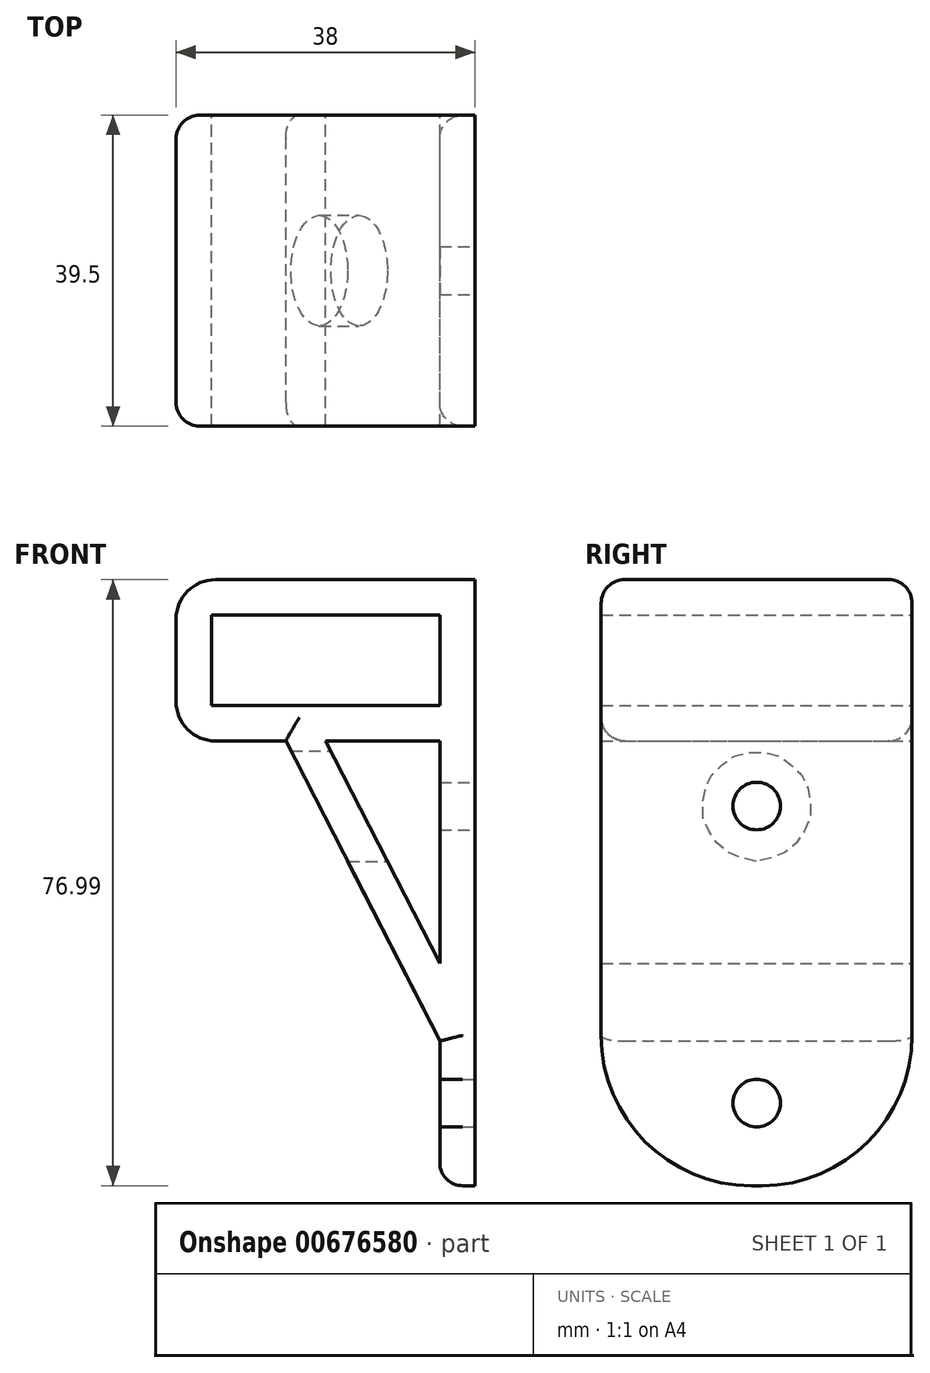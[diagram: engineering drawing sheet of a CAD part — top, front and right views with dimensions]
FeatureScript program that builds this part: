
annotation { "Feature Type Name" : "Feature", "Feature Type Description" : "" }
export const myFeature = defineFeature(function(context is Context, id is Id, definition is map)
    precondition{}
    {
        {
            var Q0;
            Q0=qCreatedBy(makeId("Front.planeOp"),FACE);
            var sketch = newSketch(context, id + "F0", { "sketchPlane" : qUnion([Q0])});
            skLineSegment(sketch, "E0.bottom", {"start": v(14.5, -5.75) * mm, "end": v(-14.5, -5.75) * mm});
            skLineSegment(sketch, "E0.top", {"start": v(14.5, 5.75) * mm, "end": v(-14.5, 5.75) * mm});
            skLineSegment(sketch, "E0.left", {"start": v(14.5, -5.75) * mm, "end": v(14.5, 5.75) * mm});
            skLineSegment(sketch, "E0.right", {"start": v(-14.5, -5.75) * mm, "end": v(-14.5, 5.75) * mm});
            skPoint(sketch, "E0.middle", {"position": v(0, 0) * mm});
            skLineSegment(sketch, "E1.0", {"start": v(19, 10.25) * mm, "end": v(-19, 10.25) * mm});
            skLineSegment(sketch, "E1.1", {"start": v(19, -10.25) * mm, "end": v(19, 10.25) * mm});
            skLineSegment(sketch, "E1.2", {"start": v(19, -10.25) * mm, "end": v(-19, -10.25) * mm});
            skLineSegment(sketch, "E1.3", {"start": v(-19, -10.25) * mm, "end": v(-19, 10.25) * mm});
            skLineSegment(sketch, "E2", {"start": v(19, -10.25) * mm, "end": v(19, -66.74) * mm});
            skLineSegment(sketch, "E3.0", {"start": v(14.5, -10.25) * mm, "end": v(14.5, -66.74) * mm});
            skLineSegment(sketch, "E4", {"start": v(14.5, -66.74) * mm, "end": v(19, -66.74) * mm});
            skLineSegment(sketch, "E5", {"start": v(14.5, -38.5) * mm, "end": v(0, -10.25) * mm});
            skLineSegment(sketch, "E6.0", {"start": v(10.5, -40.55) * mm, "end": v(-4, -12.3) * mm});
            skLineSegment(sketch, "E7", {"start": v(10.5, -40.55) * mm, "end": v(14.5, -48.35) * mm});
            skLineSegment(sketch, "E8", {"start": v(14.5, -48.35) * mm, "end": v(-4, -12.3) * mm});
            skLineSegment(sketch, "E9", {"start": v(-4, -12.3) * mm, "end": v(-5.06, -10.25) * mm});
            skSolve(sketch);
        }
        {
            var Q0;
            Q0 = qSketchRegion(id + "F0", true);
            extrude(context, id + "F1", {"entities" : qUnion([Q0]), "depth" : 39.5 * mm, "offsetDistance" : 25 * mm});
        }
        {
            var Q0;
            Q0=makeQuery(id+"F1.opExtrude","SWEPT_FACE",FACE,{"disambiguationData":[OSD([sQuery(id+"F0.wireOp",EDGE,"E1.1"),sQuery(id+"F0.wireOp",EDGE,"E2")])]});
            var sketch = newSketch(context, id + "F2", { "sketchPlane" : qUnion([Q0])});
            skLineSegment(sketch, "E10", {"start": v(-19.75, 10.25) * mm, "end": v(-19.75, -66.74) * mm, "construction": true});
            skCircle(sketch, "E11", {"center": v(-19.75, -18.51) * mm, "radius": 3.02 * mm});
            skCircle(sketch, "E12", {"center": v(-19.75, -56.24) * mm, "radius": 3.02 * mm});
            skSolve(sketch);
        }
        {
            var Q0;
            Q0 = qSketchRegion(id + "F2", true);
            extrude(context, id + "F3", {"entities" : qUnion([Q0]), "operationType" : NewBodyOperationType.REMOVE, "endBound" : BoundingType.THROUGH_ALL, "oppositeDirection" : true, "depth" : 25 * mm, "offsetDistance" : 25 * mm});
        }
        {
            var Q0;
            {var subQ0=sQuery(id+"F0.wireOp",EDGE,"E3.0");Q0=makeQuery(id+"F1.opExtrude","SWEPT_FACE",FACE,{"disambiguationData":[OSD([subQ0]),TDD([makeQuery(id+"F0.imprint","IMPRINT",EDGE,{"disambiguationData":[TD([[makeQuery(id+"F0.imprint","INTERSECT",VERTEX,{"derivedFrom":[sQuery(id+"F0.wireOp",EDGE,"E1.2"),subQ0]}),-1.0]])],"derivedFrom":subQ0})])]});}
            var sketch = newSketch(context, id + "F4", { "sketchPlane" : qUnion([Q0])});
            skCircle(sketch, "E13.0", {"center": v(19.75, -18.51) * mm, "radius": 7.02 * mm});
            skSolve(sketch);
        }
        {
            var Q0;
            Q0 = qSketchRegion(id + "F4", true);
            extrude(context, id + "F5", {"entities" : qUnion([Q0]), "operationType" : NewBodyOperationType.REMOVE, "depth" : 25 * mm, "offsetDistance" : 25 * mm});
        }
        {
            var Q0;
            Q0=makeQuery(id+"F1.opExtrude","CAP_EDGE",EDGE,{"disambiguationData":[OSD([sQuery(id+"F0.wireOp",EDGE,"E4")])],"isStart":false});
            var Q1;
            Q1=makeQuery(id+"F1.opExtrude","CAP_EDGE",EDGE,{"disambiguationData":[OSD([sQuery(id+"F0.wireOp",EDGE,"E4")])],"isStart":true});
            fillet(context, id + "F6", {"entities" : qUnion([Q0, Q1]), "radius" : 19.07 * mm, "tangentPropagation" : true, "allowEdgeOverflow" : false});
        }
        {
            var Q0;
            Q0=makeQuery(id+"F1.opExtrude","SWEPT_EDGE",EDGE,{"disambiguationData":[OSD([sQuery(id+"F0.wireOp",EDGE,"E1.2"),sQuery(id+"F0.wireOp",EDGE,"E1.3")])]});
            var Q1;
            Q1=makeQuery(id+"F1.opExtrude","SWEPT_EDGE",EDGE,{"disambiguationData":[OSD([sQuery(id+"F0.wireOp",EDGE,"E1.0"),sQuery(id+"F0.wireOp",EDGE,"E1.3")])]});
            fillet(context, id + "F7", {"entities" : qUnion([Q0, Q1]), "radius" : 5 * mm, "tangentPropagation" : true, "allowEdgeOverflow" : false});
        }
        {
            var Q0;
            {var subQ0=sQuery(id+"F0.wireOp",EDGE,"E4");var subQ1=sQuery(id+"F0.wireOp",EDGE,"E3.0");Q0=makeQuery(id+"F6.opFillet","BLEND_EDGE",EDGE,{"blendedFrom":[makeQuery(id+"F1.opExtrude","CAP_EDGE",EDGE,{"disambiguationData":[OSD([subQ0])],"isStart":true}),makeQuery(id+"F1.opExtrude","SWEPT_FACE",FACE,{"disambiguationData":[OSD([subQ1]),TDD([makeQuery(id+"F0.imprint","IMPRINT",EDGE,{"disambiguationData":[TD([[makeQuery(id+"F0.imprint","INTERSECT",VERTEX,{"derivedFrom":[subQ1,subQ0]}),1.0]])],"derivedFrom":subQ1})])]})],"blendedInto":[makeQuery(id+"F1.opExtrude","SWEPT_FACE",FACE,{"disambiguationData":[OSD([subQ1]),TDD([makeQuery(id+"F0.imprint","IMPRINT",EDGE,{"disambiguationData":[TD([[makeQuery(id+"F0.imprint","INTERSECT",VERTEX,{"derivedFrom":[subQ1,subQ0]}),1.0]])],"derivedFrom":subQ1})])]})]});}
            var Q1;
            Q1=makeQuery(id+"F1.opExtrude","CAP_EDGE",EDGE,{"disambiguationData":[OSD([sQuery(id+"F0.wireOp",EDGE,"E8"),sQuery(id+"F0.wireOp",EDGE,"E9")])],"isStart":true});
            var Q2;
            Q2=makeQuery(id+"F1.opExtrude","CAP_EDGE",EDGE,{"disambiguationData":[OSD([sQuery(id+"F0.wireOp",EDGE,"E8"),sQuery(id+"F0.wireOp",EDGE,"E9")])],"isStart":false});
            fillet(context, id + "F8", {"entities" : qUnion([Q0, Q1, Q2]), "radius" : 2.9 * mm, "tangentPropagation" : true, "allowEdgeOverflow" : false});
        }
        {
            var Q0;
            Q0=makeQuery(id+"F1.opExtrude","CAP_EDGE",EDGE,{"disambiguationData":[OSD([sQuery(id+"F0.wireOp",EDGE,"E1.0")])],"isStart":true});
            var Q1;
            Q1=makeQuery(id+"F1.opExtrude","CAP_EDGE",EDGE,{"disambiguationData":[OSD([sQuery(id+"F0.wireOp",EDGE,"E1.3")])],"isStart":false});
            fillet(context, id + "F9", {"entities" : qUnion([Q0, Q1]), "radius" : 3 * mm, "tangentPropagation" : true, "allowEdgeOverflow" : false});
        }
    });
